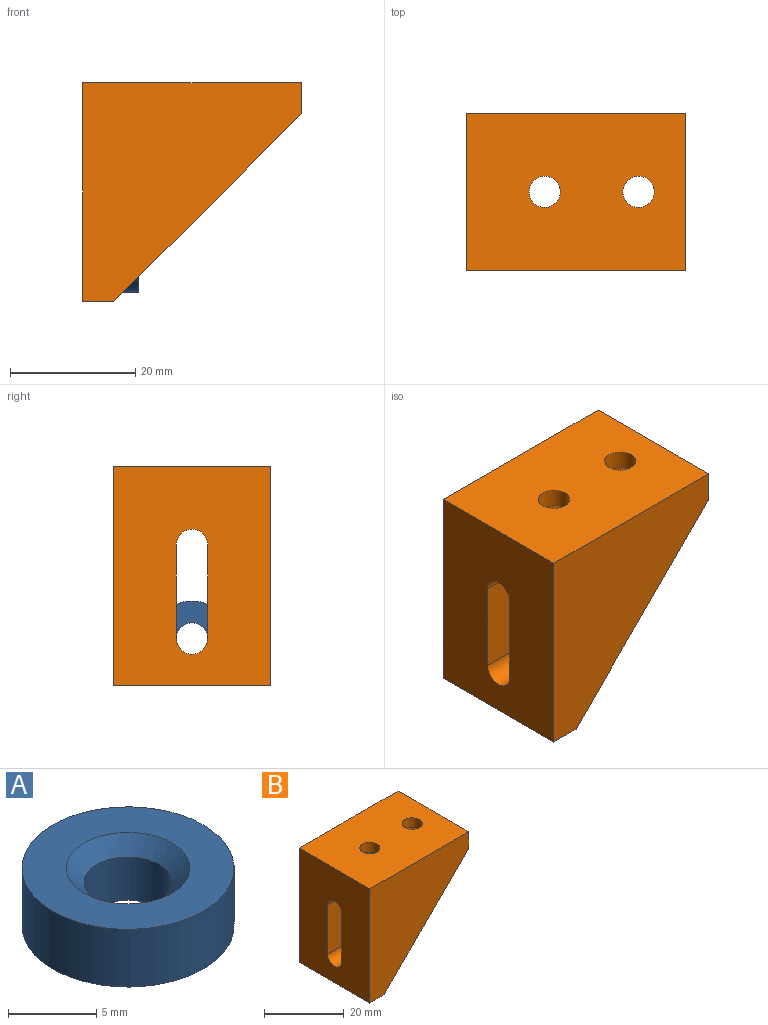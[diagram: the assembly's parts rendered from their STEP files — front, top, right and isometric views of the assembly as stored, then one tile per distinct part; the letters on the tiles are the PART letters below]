
ASSEMBLY  parts=2 mates=1
PART A: 5 faces, bbox 12x12x4 mm
  f0: cylinder r=2.5mm len=5mm, axis (0,0,-1), area 47.1mm2, adj f3,f4
  f1: cylinder r=6mm len=12mm, axis (0,0,-1), area 150.8mm2, adj f2,f3
  f2: plane 12x12mm, normal (0,0,1), area 74.6mm2, adj f1,f4
  f3: plane 12x12mm, normal (0,0,-1), area 93.5mm2, adj f0,f1
  f4: cone r=2.5mm half-angle=45deg, axis (0,0,1), area 26.7mm2, adj f0,f2
PART B: 18 faces, bbox 35x25x35 mm
  f0: plane 30x20mm, normal (1,0,0), area 505.4mm2, adj f1,f3,f7,f9,f10,f11,f12,f13
  f1: plane 30x20mm, normal (0,0,-1), area 472.8mm2, adj f0,f4,f7,f9,f16,f17
  f2: plane 35x25mm, normal (-1,0,0), area 780.4mm2, adj f3,f5,f6,f7,f10,f11,f12,f13
  f3: plane 25x5mm, normal (0,0,-1), area 125mm2, adj f0,f2,f6,f7,f8
  f4: plane 25x5mm, normal (1,0,0), area 125mm2, adj f1,f5,f6,f7,f8
  f5: plane 35x25mm, normal (0,0,1), area 835.7mm2, adj f2,f4,f6,f7,f14,f15
  f6: plane 35x35mm, normal (0,-1,0), area 775mm2, adj f2,f3,f4,f5,f8
  f7: plane 35x35mm, normal (0,1,0), area 325mm2, adj f0,f1,f2,f3,f4,f5
  f8: plane 30x30mm, normal (0.71,0,-0.71), area 212.1mm2, adj f3,f4,f6,f9
  f9: plane 30x30mm, normal (0,1,0), area 450mm2, adj f0,f1,f8
  f10: cylinder r=2.5mm len=5mm, axis (1,0,0), area 39.3mm2, adj f0,f2,f11,f13
  f11: plane 15x5mm, normal (0,1,0), area 75mm2, adj f0,f2,f10,f12
  f12: cylinder r=2.5mm len=5mm, axis (1,0,0), area 39.3mm2, adj f0,f2,f11,f13
  f13: plane 15x5mm, normal (0,-1,0), area 75mm2, adj f0,f2,f10,f12
  f14: cylinder r=2.5mm len=5mm, axis (0,0,-1), area 47.1mm2, adj f5,f16
  f15: cylinder r=2.5mm len=5mm, axis (0,0,-1), area 47.1mm2, adj f5,f17
  f16: cone r=2.5mm half-angle=45deg, axis (0,0,-1), area 62.2mm2, adj f1,f14
  f17: cone r=2.5mm half-angle=45deg, axis (0,0,-1), area 62.2mm2, adj f1,f15
PLACE A rot(axis=(0,1,0),90deg) t=(5,0,-27.5)mm
PLACE B at identity
MATE fastened A.f0 <-> B.f12  axis (-1,0,0) through (5,0,-27.5)mm
